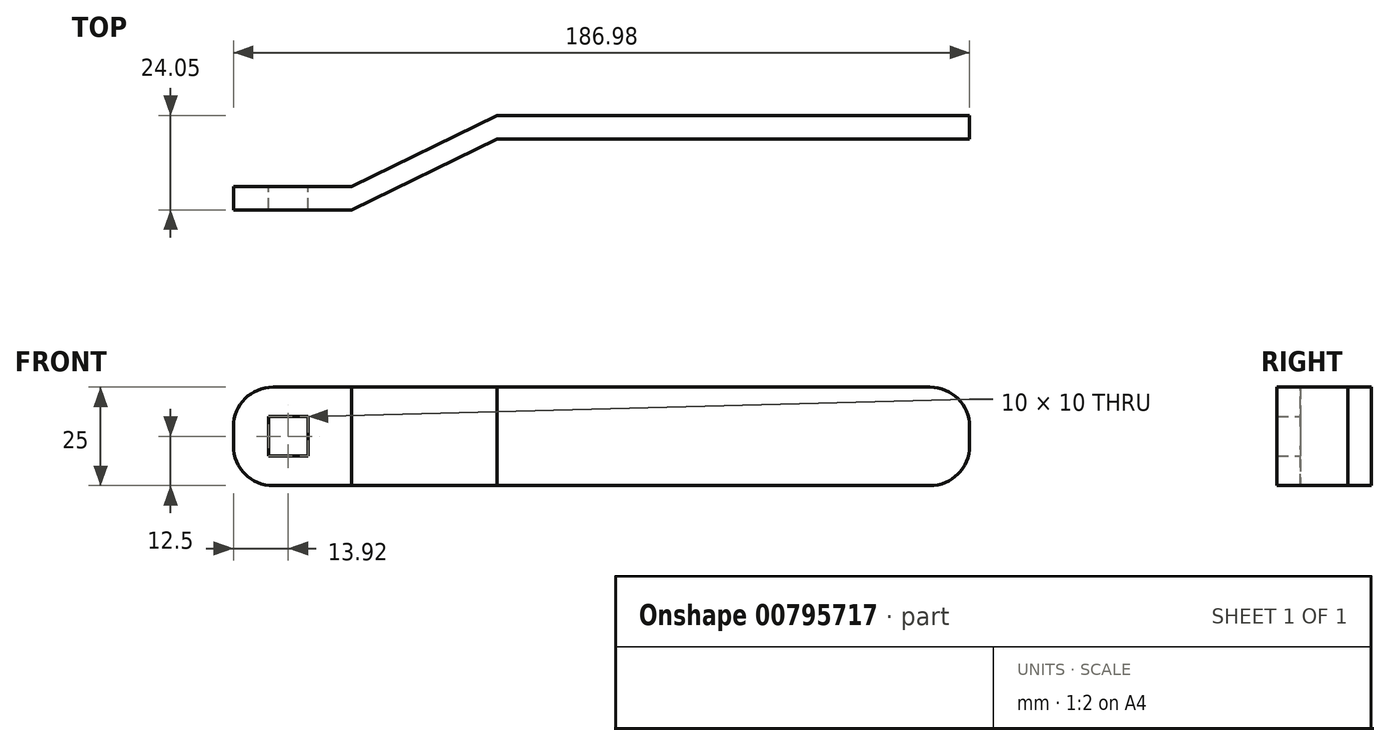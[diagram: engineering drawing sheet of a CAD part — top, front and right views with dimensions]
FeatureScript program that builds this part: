
annotation { "Feature Type Name" : "Feature", "Feature Type Description" : "" }
export const myFeature = defineFeature(function(context is Context, id is Id, definition is map)
    precondition{}
    {
        {
            var Q0;
            Q0=qCreatedBy(makeId("Top.planeOp"),FACE);
            var sketch = newSketch(context, id + "F0", { "sketchPlane" : qUnion([Q0])});
            skLineSegment(sketch, "E0", {"start": v(-13.92, 2.92) * mm, "end": v(-13.92, -3.08) * mm});
            skLineSegment(sketch, "E1", {"start": v(-13.92, -3.08) * mm, "end": v(16.08, -3.08) * mm});
            skLineSegment(sketch, "E2", {"start": v(16.08, -3.08) * mm, "end": v(53.06, 14.97) * mm});
            skLineSegment(sketch, "E3", {"start": v(53.06, 14.97) * mm, "end": v(173.06, 14.97) * mm});
            skLineSegment(sketch, "E4", {"start": v(173.06, 14.97) * mm, "end": v(173.06, 20.97) * mm});
            skLineSegment(sketch, "E5", {"start": v(173.06, 20.97) * mm, "end": v(53.06, 20.97) * mm});
            skLineSegment(sketch, "E6", {"start": v(-13.92, 2.92) * mm, "end": v(16.08, 2.92) * mm});
            skLineSegment(sketch, "E7", {"start": v(16.08, 2.92) * mm, "end": v(53.06, 20.97) * mm});
            skLineSegment(sketch, "E8", {"start": v(53.06, 20.97) * mm, "end": v(53.06, 20.97) * mm});
            skSolve(sketch);
        }
        {
            var Q0;
            Q0=makeQuery(id+"F0.imprint","IMPRINT",FACE,{"disambiguationData":[TD([[makeQuery(id+"F0.imprint","IMPRINT",EDGE,{"derivedFrom":sQuery(id+"F0.wireOp",EDGE,"E0")}),1.0]])]});
            extrude(context, id + "F1", {"entities" : qUnion([Q0]), "endBound" : BoundingType.SYMMETRIC, "depth" : 25 * mm, "offsetDistance" : 25 * mm});
        }
        {
            var Q0;
            Q0=makeQuery(id+"F1.opExtrude","CAP_EDGE",EDGE,{"disambiguationData":[OSD([sQuery(id+"F0.wireOp",EDGE,"E0")])],"isStart":false});
            fillet(context, id + "F2", {"entities" : qUnion([Q0]), "radius" : 10 * mm, "tangentPropagation" : true, "allowEdgeOverflow" : false});
        }
        {
            var Q0;
            Q0=makeQuery(id+"F1.opExtrude","CAP_EDGE",EDGE,{"disambiguationData":[OSD([sQuery(id+"F0.wireOp",EDGE,"E0")])],"isStart":true});
            var Q1;
            Q1=makeQuery(id+"F1.opExtrude","CAP_EDGE",EDGE,{"disambiguationData":[OSD([sQuery(id+"F0.wireOp",EDGE,"E4")])],"isStart":false});
            var Q2;
            Q2=makeQuery(id+"F1.opExtrude","CAP_EDGE",EDGE,{"disambiguationData":[OSD([sQuery(id+"F0.wireOp",EDGE,"E4")])],"isStart":true});
            fillet(context, id + "F3", {"entities" : qUnion([Q0, Q1, Q2]), "radius" : 10 * mm, "tangentPropagation" : true, "allowEdgeOverflow" : false});
        }
        {
            var Q0;
            Q0=makeQuery(id+"F1.opExtrude","SWEPT_FACE",FACE,{"disambiguationData":[OSD([sQuery(id+"F0.wireOp",EDGE,"E6")])]});
            var sketch = newSketch(context, id + "F4", { "sketchPlane" : qUnion([Q0])});
            skLineSegment(sketch, "E9.bottom", {"start": v(-5, 5) * mm, "end": v(5, 5) * mm});
            skLineSegment(sketch, "E9.top", {"start": v(-5, -5) * mm, "end": v(5, -5) * mm});
            skLineSegment(sketch, "E9.left", {"start": v(-5, 5) * mm, "end": v(-5, -5) * mm});
            skLineSegment(sketch, "E9.right", {"start": v(5, 5) * mm, "end": v(5, -5) * mm});
            skPoint(sketch, "E9.middle", {"position": v(0, 0) * mm});
            skSolve(sketch);
        }
        {
            var Q0;
            Q0=makeQuery(id+"F4.imprint","IMPRINT",FACE,{"disambiguationData":[TD([[makeQuery(id+"F4.imprint","IMPRINT",EDGE,{"derivedFrom":sQuery(id+"F4.wireOp",EDGE,"E9.bottom")}),-1.0]])]});
            extrude(context, id + "F5", {"entities" : qUnion([Q0]), "operationType" : NewBodyOperationType.REMOVE, "endBound" : BoundingType.UP_TO_NEXT, "oppositeDirection" : true, "depth" : 25 * mm, "offsetDistance" : 25 * mm});
        }
    });
